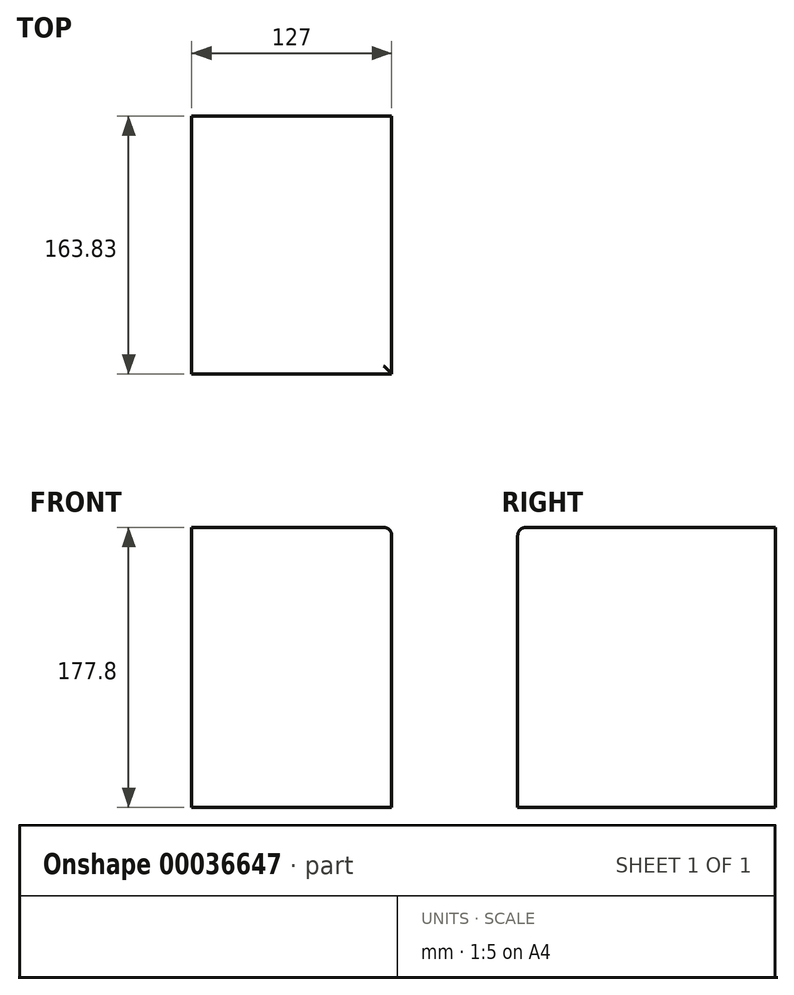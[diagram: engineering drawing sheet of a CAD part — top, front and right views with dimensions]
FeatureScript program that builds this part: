
annotation { "Feature Type Name" : "Feature", "Feature Type Description" : "" }
export const myFeature = defineFeature(function(context is Context, id is Id, definition is map)
    precondition{}
    {
        {
            var Q0;
            Q0=qCreatedBy(makeId("Top.planeOp"),FACE);
            var sketch = newSketch(context, id + "F0", { "sketchPlane" : qUnion([Q0])});
            skLineSegment(sketch, "E0.bottom", {"start": v(0, 0) * mm, "end": v(127, 0) * mm});
            skLineSegment(sketch, "E0.top", {"start": v(0, 163.83) * mm, "end": v(127, 163.83) * mm});
            skLineSegment(sketch, "E0.left", {"start": v(0, 0) * mm, "end": v(0, 163.83) * mm});
            skLineSegment(sketch, "E0.right", {"start": v(127, 0) * mm, "end": v(127, 163.83) * mm});
            skSolve(sketch);
        }
        {
            var Q0;
            Q0 = qSketchRegion(id + "F0", true);
            extrude(context, id + "F1", {"entities" : qUnion([Q0]), "depth" : 177.8 * mm});
        }
        {
            var Q0;
            Q0=makeQuery(id+"F1.opExtrude","CAP_EDGE",EDGE,{"disambiguationData":[OSD([sQuery(id+"F0.wireOp",EDGE,"E0.bottom")])],"isStart":false});
            var Q1;
            Q1=makeQuery(id+"F1.opExtrude","CAP_EDGE",EDGE,{"disambiguationData":[OSD([sQuery(id+"F0.wireOp",EDGE,"E0.right")])],"isStart":false});
            fillet(context, id + "F2", {"entities" : qUnion([Q0, Q1]), "radius" : 5.08 * mm, "tangentPropagation" : true, "allowEdgeOverflow" : false});
        }
    });
